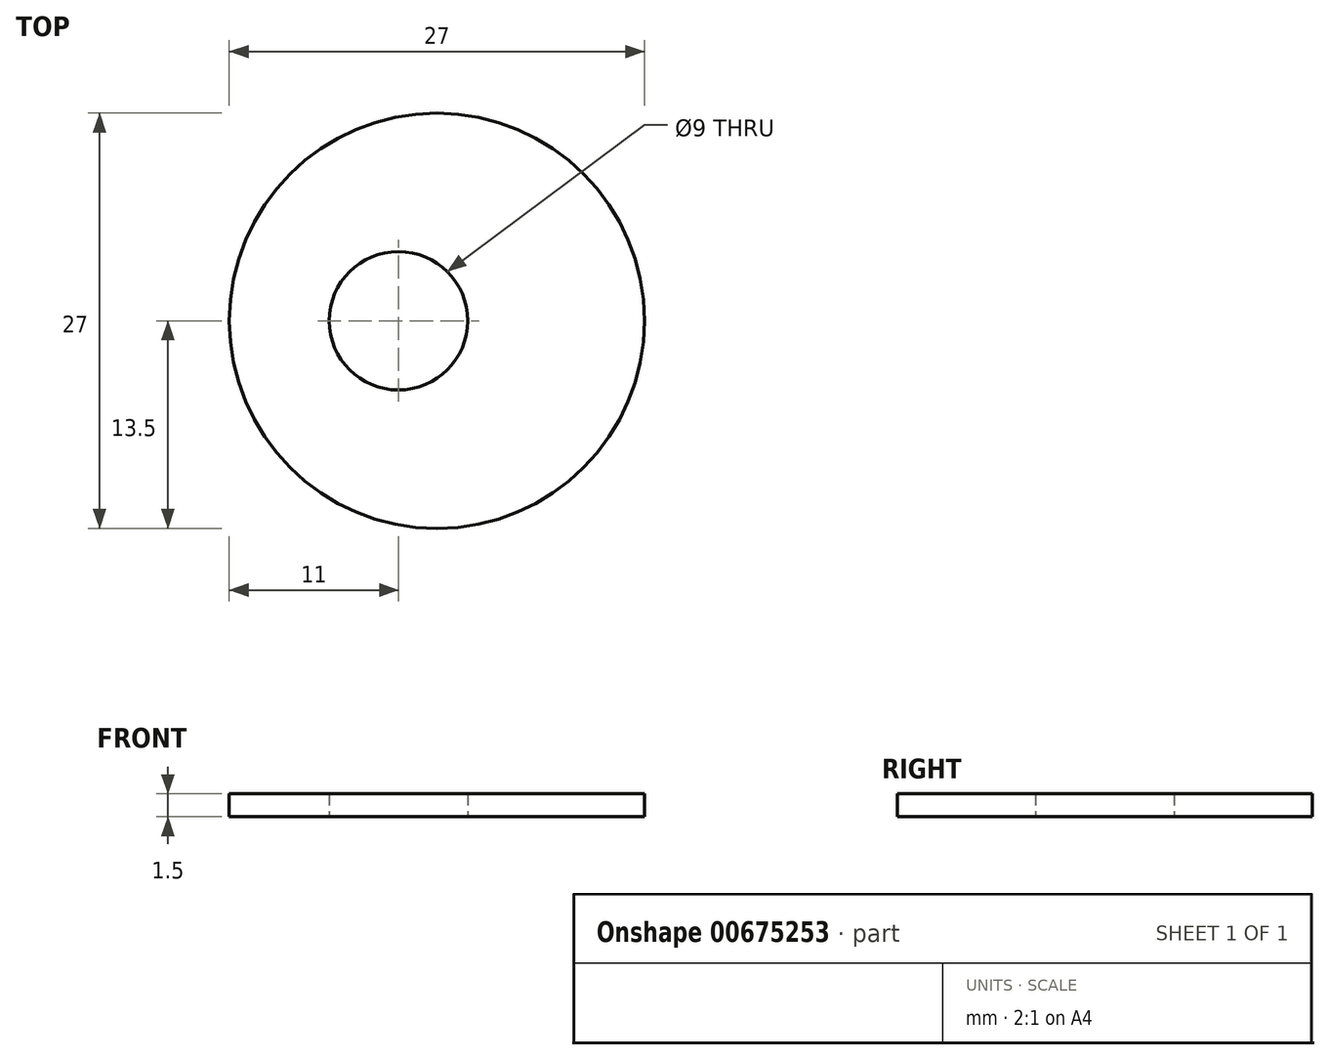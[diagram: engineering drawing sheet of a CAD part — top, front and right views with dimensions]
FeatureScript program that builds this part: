
annotation { "Feature Type Name" : "Feature", "Feature Type Description" : "" }
export const myFeature = defineFeature(function(context is Context, id is Id, definition is map)
    precondition{}
    {
        {
            var Q0;
            Q0=qCreatedBy(makeId("Top.planeOp"),FACE);
            var sketch = newSketch(context, id + "F0", { "sketchPlane" : qUnion([Q0])});
            skCircle(sketch, "E0", {"center": v(0, 0) * mm, "radius": 13.5 * mm});
            skCircle(sketch, "E1", {"center": v(0, 0) * mm, "radius": 3.75 * mm});
            skCircle(sketch, "E2", {"center": v(-2.5, 0) * mm, "radius": 4.5 * mm});
            skPoint(sketch, "E3", {"position": v(-13.5, 0) * mm});
            skPoint(sketch, "E4", {"position": v(-2.5, 13.27) * mm});
            skSolve(sketch);
        }
        {
            var Q0;
            Q0=makeQuery(id+"F0.imprint","IMPRINT",FACE,{"disambiguationData":[TD([[makeQuery(id+"F0.imprint","IMPRINT",EDGE,{"derivedFrom":sQuery(id+"F0.wireOp",EDGE,"E0")}),1.0]])]});
            var Q1;
            {var subQ0=sQuery(id+"F0.wireOp",EDGE,"E2");var subQ1=sQuery(id+"F0.wireOp",EDGE,"E1");var subQ2=makeQuery(id+"F0.imprint","INTERSECT",VERTEX,{"disambiguationData":[OD(0.0)],"derivedFrom":[subQ1,subQ0]});Q1=makeQuery(id+"F0.imprint","IMPRINT",FACE,{"disambiguationData":[TD([[makeQuery(id+"F0.imprint","IMPRINT",EDGE,{"disambiguationData":[TD([[subQ2,-1.0]])],"derivedFrom":subQ1}),1.0]])]});}
            extrude(context, id + "F1", {"entities" : qUnion([Q0, Q1]), "depth" : 1.5 * mm, "offsetDistance" : 25 * mm});
        }
    });
